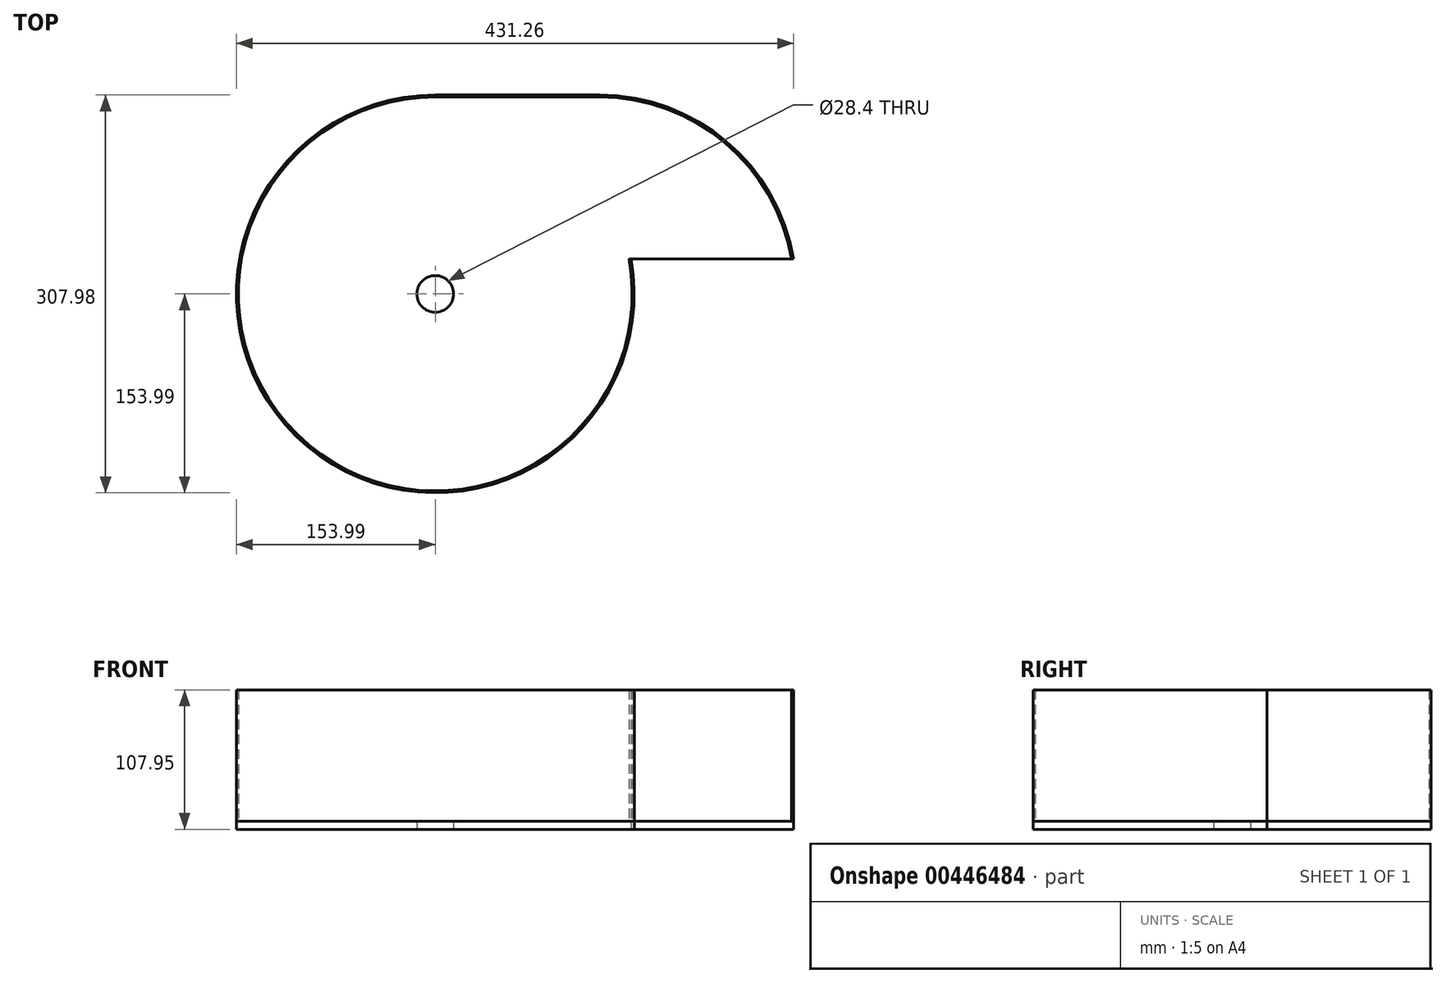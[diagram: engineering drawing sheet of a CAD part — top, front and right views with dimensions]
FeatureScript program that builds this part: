
annotation { "Feature Type Name" : "Feature", "Feature Type Description" : "" }
export const myFeature = defineFeature(function(context is Context, id is Id, definition is map)
    precondition{}
    {
        {
            var Q0;
            Q0=qCreatedBy(makeId("Top.planeOp"),FACE);
            var sketch = newSketch(context, id + "F0", { "sketchPlane" : qUnion([Q0])});
            skArc(sketch, "E0", {"start": v(0, 153.99) * mm, "mid": v(-98.88, -118.04) * mm, "end": v(151.6, 26.99) * mm});
            skLineSegment(sketch, "E1", {"start": v(0, 153.99) * mm, "end": v(127, 153.99) * mm});
            skLineSegment(sketch, "E2", {"start": v(277.27, 26.99) * mm, "end": v(151.6, 26.99) * mm});
            skPoint(sketch, "E3.visualSharp", {"position": v(279.4, 153.99) * mm});
            skArc(sketch, "E3.filletArc", {"start": v(277.27, 26.99) * mm, "mid": v(225.37, 117.98) * mm, "end": v(127, 153.99) * mm});
            skSolve(sketch);
        }
        {
            var Q0;
            Q0=makeQuery(id+"F0.imprint","IMPRINT",FACE,{"disambiguationData":[TD([[makeQuery(id+"F0.imprint","IMPRINT",EDGE,{"derivedFrom":sQuery(id+"F0.wireOp",EDGE,"E0")}),1.0]])]});
            extrude(context, id + "F1", {"entities" : qUnion([Q0]), "depth" : 6.35 * mm});
        }
        {
            var Q0;
            Q0=makeQuery(id+"F1.opExtrude","CAP_FACE",FACE,{"disambiguationData":[OSD([sQuery(id+"F0.wireOp",EDGE,"E0"),sQuery(id+"F0.wireOp",EDGE,"E1"),sQuery(id+"F0.wireOp",EDGE,"E2"),sQuery(id+"F0.wireOp",EDGE,"E3.filletArc")])],"isStart":false});
            var sketch = newSketch(context, id + "F2", { "sketchPlane" : qUnion([Q0])});
            skPoint(sketch, "E4", {"position": v(0, 0) * mm});
            skSolve(sketch);
        }
        {
            var Q0;
            Q0=sQuery(id+"F2.wireOp",VERTEX,"E4");
            var Q1;
            Q1=makeQuery(id+"F1.opExtrude","SWEPT_BODY",BODY,{"disambiguationData":[OSD([sQuery(id+"F0.wireOp",EDGE,"E0"),sQuery(id+"F0.wireOp",EDGE,"E1"),sQuery(id+"F0.wireOp",EDGE,"E2"),sQuery(id+"F0.wireOp",EDGE,"E3.filletArc")])]});
            hole(context, id + "F3", {"style" : HoleStyle.SIMPLE, "endStyle" : HoleEndStyle.THROUGH, "holeDiameter" : 28.4 * mm, "isTappedThrough" : true, "tappedDepth" : 12.7 * mm, "tapClearance" : 3, "locations" : qUnion([Q0]), "scope" : qUnion([Q1]), "startStyle" : HoleStartStyle.PART});
        }
        {
            var Q0;
            Q0=makeQuery(id+"F1.opExtrude","CAP_FACE",FACE,{"disambiguationData":[OSD([sQuery(id+"F0.wireOp",EDGE,"E0"),sQuery(id+"F0.wireOp",EDGE,"E1"),sQuery(id+"F0.wireOp",EDGE,"E2"),sQuery(id+"F0.wireOp",EDGE,"E3.filletArc")])],"isStart":false});
            var sketch = newSketch(context, id + "F4", { "sketchPlane" : qUnion([Q0])});
            skArc(sketch, "E5.0", {"start": v(0, 152.4) * mm, "mid": v(-97.76, -116.92) * mm, "end": v(150, 26.99) * mm});
            skLineSegment(sketch, "E5.1", {"start": v(0, 152.4) * mm, "end": v(127, 152.4) * mm});
            skArc(sketch, "E5.2", {"start": v(275.66, 26.99) * mm, "mid": v(224.25, 116.86) * mm, "end": v(127, 152.4) * mm});
            skLineSegment(sketch, "E6", {"start": v(150, 26.99) * mm, "end": v(151.6, 26.99) * mm});
            skLineSegment(sketch, "E7", {"start": v(275.66, 26.99) * mm, "end": v(277.27, 26.99) * mm});
            skSolve(sketch);
        }
        {
            var Q0;
            Q0=makeQuery(id+"F4.imprint","IMPRINT",FACE,{"disambiguationData":[TD([[makeQuery(id+"F4.imprint","IMPRINT",EDGE,{"derivedFrom":sQuery(id+"F4.wireOp",EDGE,"E5.0")}),-1.0]])]});
            extrude(context, id + "F5", {"entities" : qUnion([Q0]), "depth" : 101.6 * mm});
        }
    });
